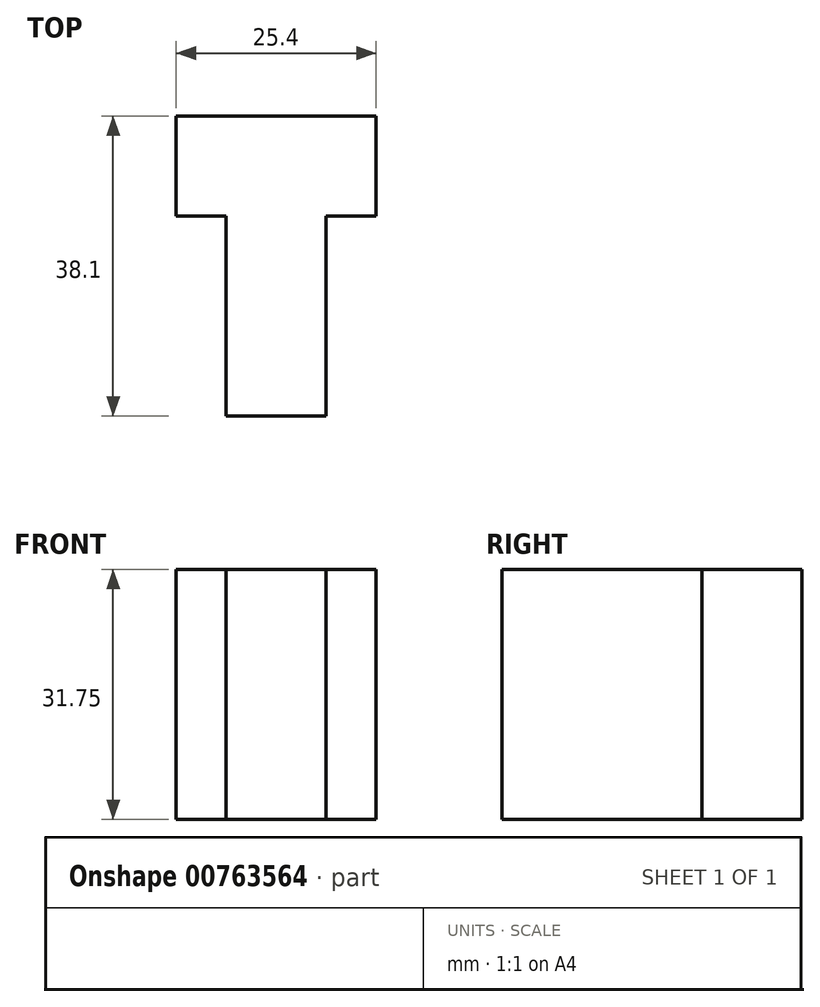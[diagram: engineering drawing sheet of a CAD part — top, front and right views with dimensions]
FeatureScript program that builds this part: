
annotation { "Feature Type Name" : "Feature", "Feature Type Description" : "" }
export const myFeature = defineFeature(function(context is Context, id is Id, definition is map)
    precondition{}
    {
        {
            var Q0;
            Q0=qCreatedBy(makeId("Top.planeOp"),FACE);
            var sketch = newSketch(context, id + "F0", { "sketchPlane" : qUnion([Q0])});
            skLineSegment(sketch, "E0", {"start": v(0, 0) * mm, "end": v(25.4, 0) * mm});
            skLineSegment(sketch, "E1", {"start": v(25.4, 0) * mm, "end": v(25.4, -12.7) * mm});
            skLineSegment(sketch, "E2", {"start": v(25.4, -12.7) * mm, "end": v(19.05, -12.7) * mm});
            skLineSegment(sketch, "E3", {"start": v(19.05, -12.7) * mm, "end": v(19.05, -38.1) * mm});
            skLineSegment(sketch, "E4", {"start": v(19.05, -38.1) * mm, "end": v(6.35, -38.1) * mm});
            skLineSegment(sketch, "E5", {"start": v(6.35, -38.1) * mm, "end": v(6.35, -12.7) * mm});
            skLineSegment(sketch, "E6", {"start": v(6.35, -12.7) * mm, "end": v(0, -12.7) * mm});
            skLineSegment(sketch, "E7", {"start": v(0, 0) * mm, "end": v(0, -12.7) * mm});
            skSolve(sketch);
        }
        {
            var Q0;
            Q0 = qSketchRegion(id + "F0", true);
            extrude(context, id + "F1", {"entities" : qUnion([Q0]), "depth" : 31.75 * mm, "offsetDistance" : 25.4 * mm});
        }
    });
